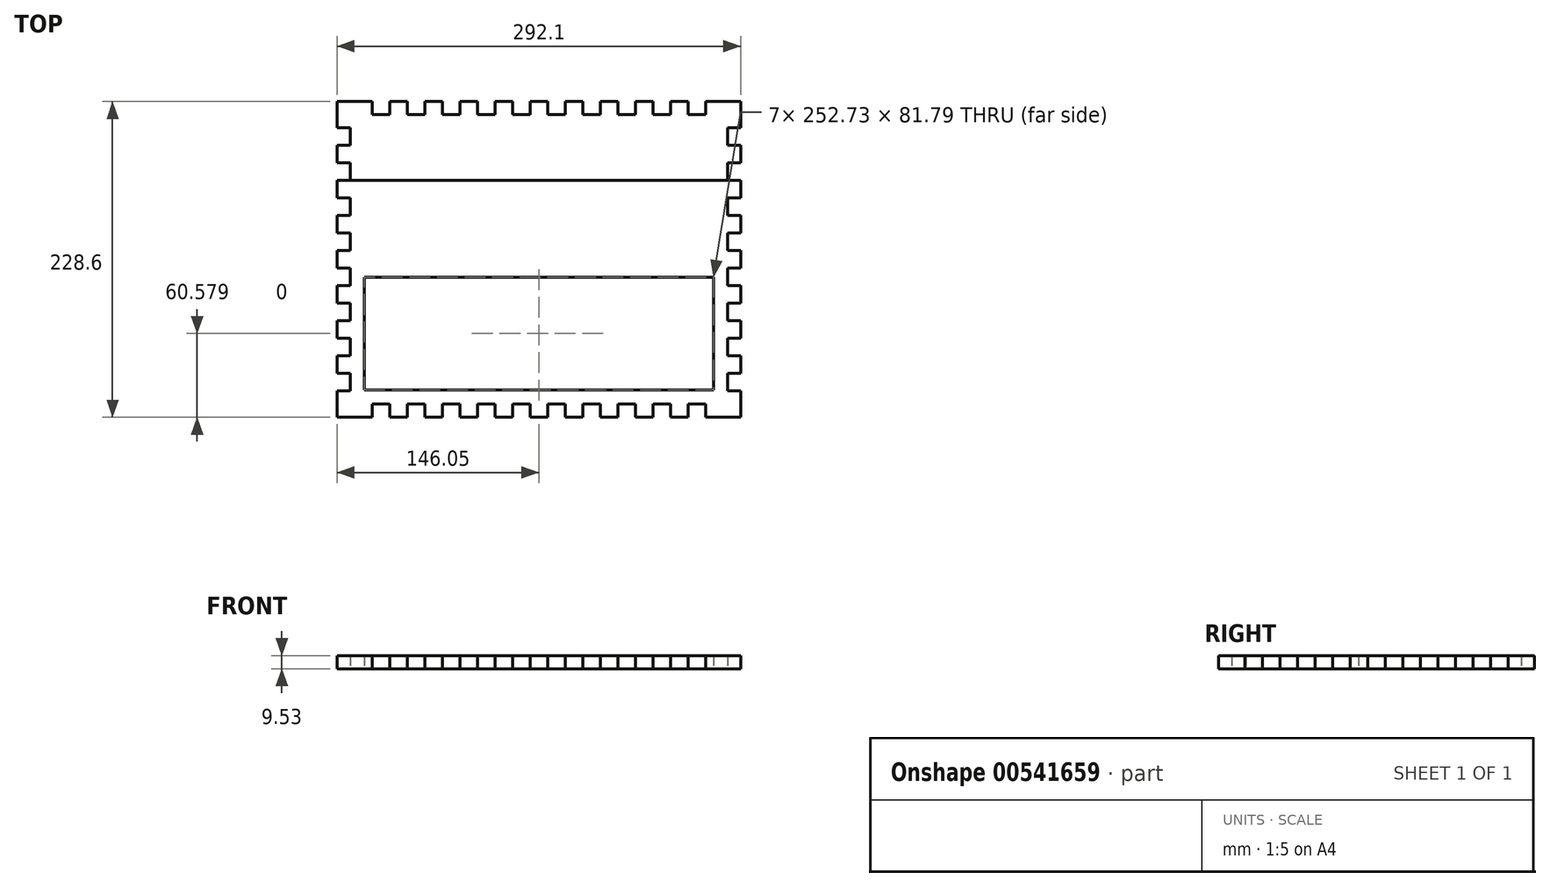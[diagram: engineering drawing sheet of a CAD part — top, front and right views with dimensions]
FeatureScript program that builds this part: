
annotation { "Feature Type Name" : "Feature", "Feature Type Description" : "" }
export const myFeature = defineFeature(function(context is Context, id is Id, definition is map)
    precondition{}
    {
        {
            var Q0;
            Q0=qCreatedBy(makeId("Top.planeOp"),FACE);
            var sketch = newSketch(context, id + "F0", { "sketchPlane" : qUnion([Q0])});
            skLineSegment(sketch, "E0.bottom", {"start": v(0, 0) * mm, "end": v(25.4, 0) * mm});
            skLineSegment(sketch, "E0.left", {"start": v(0, 0) * mm, "end": v(0, -19.05) * mm});
            skLineSegment(sketch, "E1", {"start": v(25.4, 0) * mm, "end": v(25.4, -9.53) * mm});
            skLineSegment(sketch, "E2", {"start": v(25.4, -9.53) * mm, "end": v(38.1, -9.53) * mm});
            skLineSegment(sketch, "E3", {"start": v(38.1, -9.53) * mm, "end": v(38.1, 0) * mm});
            skLineSegment(sketch, "E4", {"start": v(38.1, 0) * mm, "end": v(50.8, 0) * mm});
            skLineSegment(sketch, "E5", {"start": v(50.8, 0) * mm, "end": v(50.8, -9.53) * mm});
            skLineSegment(sketch, "E6", {"start": v(50.8, -9.53) * mm, "end": v(63.5, -9.53) * mm});
            skLineSegment(sketch, "E7", {"start": v(63.5, -9.53) * mm, "end": v(63.5, 0) * mm});
            skLineSegment(sketch, "E8", {"start": v(63.5, 0) * mm, "end": v(76.2, 0) * mm});
            skLineSegment(sketch, "E9", {"start": v(76.2, 0) * mm, "end": v(76.2, -9.52) * mm});
            skLineSegment(sketch, "E10", {"start": v(76.2, -9.52) * mm, "end": v(88.9, -9.52) * mm});
            skLineSegment(sketch, "E11", {"start": v(88.9, -9.52) * mm, "end": v(88.9, 0) * mm});
            skLineSegment(sketch, "E12", {"start": v(88.9, 0) * mm, "end": v(101.6, 0) * mm});
            skLineSegment(sketch, "E13", {"start": v(101.6, 0) * mm, "end": v(101.6, -9.52) * mm});
            skLineSegment(sketch, "E14", {"start": v(101.6, -9.52) * mm, "end": v(114.3, -9.52) * mm});
            skLineSegment(sketch, "E15", {"start": v(114.3, -9.52) * mm, "end": v(114.3, 0) * mm});
            skLineSegment(sketch, "E16.trimOffspring", {"start": v(114.3, 0) * mm, "end": v(127, 0) * mm});
            skLineSegment(sketch, "E17", {"start": v(127, 0) * mm, "end": v(127, -9.53) * mm});
            skLineSegment(sketch, "E18", {"start": v(127, -9.53) * mm, "end": v(139.7, -9.53) * mm});
            skLineSegment(sketch, "E19", {"start": v(139.7, -9.53) * mm, "end": v(139.7, 0) * mm});
            skLineSegment(sketch, "E20", {"start": v(139.7, 0) * mm, "end": v(152.4, 0) * mm});
            skLineSegment(sketch, "E21", {"start": v(152.4, 0) * mm, "end": v(152.4, -9.53) * mm});
            skLineSegment(sketch, "E22", {"start": v(152.4, -9.53) * mm, "end": v(165.1, -9.53) * mm});
            skLineSegment(sketch, "E23", {"start": v(165.1, -9.53) * mm, "end": v(165.1, 0) * mm});
            skLineSegment(sketch, "E24", {"start": v(165.1, 0) * mm, "end": v(177.8, 0) * mm});
            skLineSegment(sketch, "E25", {"start": v(177.8, 0) * mm, "end": v(177.8, -9.53) * mm});
            skLineSegment(sketch, "E26", {"start": v(177.8, -9.53) * mm, "end": v(190.5, -9.53) * mm});
            skLineSegment(sketch, "E27", {"start": v(190.5, -9.53) * mm, "end": v(190.5, 0) * mm});
            skLineSegment(sketch, "E28.trimOffspring", {"start": v(190.5, 0) * mm, "end": v(203.2, 0) * mm});
            skLineSegment(sketch, "E29", {"start": v(203.2, 0) * mm, "end": v(203.2, -9.53) * mm});
            skLineSegment(sketch, "E30", {"start": v(203.2, -9.53) * mm, "end": v(215.9, -9.53) * mm});
            skLineSegment(sketch, "E31", {"start": v(215.9, -9.53) * mm, "end": v(215.9, 0) * mm});
            skLineSegment(sketch, "E32", {"start": v(215.9, 0) * mm, "end": v(228.6, 0) * mm});
            skLineSegment(sketch, "E33", {"start": v(228.6, 0) * mm, "end": v(228.6, -9.53) * mm});
            skLineSegment(sketch, "E34", {"start": v(228.6, -9.53) * mm, "end": v(241.3, -9.53) * mm});
            skLineSegment(sketch, "E35", {"start": v(241.3, -9.53) * mm, "end": v(241.3, 0) * mm});
            skLineSegment(sketch, "E36", {"start": v(241.3, 0) * mm, "end": v(254, 0) * mm});
            skLineSegment(sketch, "E37", {"start": v(254, 0) * mm, "end": v(254, -9.53) * mm});
            skLineSegment(sketch, "E38", {"start": v(254, -9.53) * mm, "end": v(266.7, -9.53) * mm});
            skLineSegment(sketch, "E39", {"start": v(266.7, -9.53) * mm, "end": v(266.7, 0) * mm});
            skLineSegment(sketch, "E40.trimOffspring", {"start": v(266.7, 0) * mm, "end": v(292.1, 0) * mm});
            skLineSegment(sketch, "E41", {"start": v(0, -19.05) * mm, "end": v(9.52, -19.05) * mm});
            skLineSegment(sketch, "E42", {"start": v(9.52, -19.05) * mm, "end": v(9.52, -31.75) * mm});
            skLineSegment(sketch, "E43", {"start": v(9.52, -31.75) * mm, "end": v(0, -31.75) * mm});
            skLineSegment(sketch, "E44", {"start": v(0, -31.75) * mm, "end": v(0, -44.45) * mm});
            skLineSegment(sketch, "E45", {"start": v(0, -44.45) * mm, "end": v(9.53, -44.45) * mm});
            skLineSegment(sketch, "E46", {"start": v(9.53, -44.45) * mm, "end": v(9.53, -57.15) * mm});
            skLineSegment(sketch, "E47", {"start": v(9.53, -57.15) * mm, "end": v(0, -57.15) * mm});
            skLineSegment(sketch, "E48", {"start": v(0, -57.15) * mm, "end": v(0, -69.85) * mm});
            skLineSegment(sketch, "E49", {"start": v(0, -69.85) * mm, "end": v(9.53, -69.85) * mm});
            skLineSegment(sketch, "E50", {"start": v(9.53, -69.85) * mm, "end": v(9.53, -82.55) * mm});
            skLineSegment(sketch, "E51", {"start": v(9.53, -82.55) * mm, "end": v(0, -82.55) * mm});
            skLineSegment(sketch, "E52", {"start": v(0, -82.55) * mm, "end": v(0, -95.25) * mm});
            skLineSegment(sketch, "E53", {"start": v(0, -95.25) * mm, "end": v(9.53, -95.25) * mm});
            skLineSegment(sketch, "E54", {"start": v(9.53, -95.25) * mm, "end": v(9.53, -107.95) * mm});
            skLineSegment(sketch, "E55", {"start": v(9.53, -107.95) * mm, "end": v(0, -107.95) * mm});
            skLineSegment(sketch, "E56.trimOffspring", {"start": v(0, -107.95) * mm, "end": v(0, -120.65) * mm});
            skLineSegment(sketch, "E57", {"start": v(0, -120.65) * mm, "end": v(9.53, -120.65) * mm});
            skLineSegment(sketch, "E58", {"start": v(9.53, -120.65) * mm, "end": v(9.53, -133.35) * mm});
            skLineSegment(sketch, "E59", {"start": v(9.53, -133.35) * mm, "end": v(0, -133.35) * mm});
            skLineSegment(sketch, "E60", {"start": v(0, -133.35) * mm, "end": v(0, -146.05) * mm});
            skLineSegment(sketch, "E61", {"start": v(0, -146.05) * mm, "end": v(9.53, -146.05) * mm});
            skLineSegment(sketch, "E62", {"start": v(9.53, -146.05) * mm, "end": v(9.53, -158.75) * mm});
            skLineSegment(sketch, "E63", {"start": v(9.53, -158.75) * mm, "end": v(0, -158.75) * mm});
            skLineSegment(sketch, "E64", {"start": v(0, -158.75) * mm, "end": v(0, -171.45) * mm});
            skLineSegment(sketch, "E65", {"start": v(0, -171.45) * mm, "end": v(9.53, -171.45) * mm});
            skLineSegment(sketch, "E66", {"start": v(9.53, -171.45) * mm, "end": v(9.53, -184.15) * mm});
            skLineSegment(sketch, "E67", {"start": v(9.53, -184.15) * mm, "end": v(0, -184.15) * mm});
            skLineSegment(sketch, "E68.trimOffspring", {"start": v(0, -184.15) * mm, "end": v(0, -196.85) * mm});
            skLineSegment(sketch, "E69", {"start": v(0, -196.85) * mm, "end": v(9.53, -196.85) * mm});
            skLineSegment(sketch, "E70", {"start": v(9.53, -196.85) * mm, "end": v(9.53, -209.55) * mm});
            skLineSegment(sketch, "E71", {"start": v(9.53, -209.55) * mm, "end": v(0, -209.55) * mm});
            skLineSegment(sketch, "E72.trimOffspring", {"start": v(0, -209.55) * mm, "end": v(0, -228.6) * mm});
            skLineSegment(sketch, "E73", {"start": v(146.05, 0) * mm, "end": v(146.05, -86.34) * mm, "construction": true});
            skLineSegment(sketch, "E74", {"start": v(0, -114.3) * mm, "end": v(52.01, -114.3) * mm, "construction": true});
            skLineSegment(sketch, "E75.MirrorCS", {"start": v(292.1, 0) * mm, "end": v(292.1, -19.05) * mm});
            skLineSegment(sketch, "E76.MirrorCS", {"start": v(292.1, -19.05) * mm, "end": v(282.57, -19.05) * mm});
            skLineSegment(sketch, "E77.MirrorCS", {"start": v(282.57, -19.05) * mm, "end": v(282.57, -31.75) * mm});
            skLineSegment(sketch, "E78.MirrorCS", {"start": v(282.57, -31.75) * mm, "end": v(292.1, -31.75) * mm});
            skLineSegment(sketch, "E79.MirrorCS", {"start": v(292.1, -31.75) * mm, "end": v(292.1, -44.45) * mm});
            skLineSegment(sketch, "E80.MirrorCS", {"start": v(292.1, -44.45) * mm, "end": v(282.57, -44.45) * mm});
            skLineSegment(sketch, "E81.MirrorCS", {"start": v(282.57, -44.45) * mm, "end": v(282.57, -57.15) * mm});
            skLineSegment(sketch, "E82.MirrorCS", {"start": v(282.57, -57.15) * mm, "end": v(292.1, -57.15) * mm});
            skLineSegment(sketch, "E83.MirrorCS", {"start": v(292.1, -57.15) * mm, "end": v(292.1, -69.85) * mm});
            skLineSegment(sketch, "E84.MirrorCS", {"start": v(292.1, -69.85) * mm, "end": v(282.57, -69.85) * mm});
            skLineSegment(sketch, "E85.MirrorCS", {"start": v(282.57, -69.85) * mm, "end": v(282.57, -82.55) * mm});
            skLineSegment(sketch, "E86.MirrorCS", {"start": v(282.57, -107.95) * mm, "end": v(292.1, -107.95) * mm});
            skLineSegment(sketch, "E87.MirrorCS", {"start": v(292.1, -107.95) * mm, "end": v(292.1, -120.65) * mm});
            skLineSegment(sketch, "E88.MirrorCS", {"start": v(292.1, -120.65) * mm, "end": v(282.57, -120.65) * mm});
            skLineSegment(sketch, "E89.MirrorCS", {"start": v(282.57, -120.65) * mm, "end": v(282.57, -133.35) * mm});
            skLineSegment(sketch, "E90.MirrorCS", {"start": v(282.57, -133.35) * mm, "end": v(292.1, -133.35) * mm});
            skLineSegment(sketch, "E91.MirrorCS", {"start": v(292.1, -133.35) * mm, "end": v(292.1, -146.05) * mm});
            skLineSegment(sketch, "E92.MirrorCS", {"start": v(292.1, -146.05) * mm, "end": v(282.57, -146.05) * mm});
            skLineSegment(sketch, "E93.MirrorCS", {"start": v(282.57, -146.05) * mm, "end": v(282.57, -158.75) * mm});
            skLineSegment(sketch, "E94.MirrorCS", {"start": v(282.57, -158.75) * mm, "end": v(292.1, -158.75) * mm});
            skLineSegment(sketch, "E95.MirrorCS", {"start": v(292.1, -158.75) * mm, "end": v(292.1, -171.45) * mm});
            skLineSegment(sketch, "E96.MirrorCS", {"start": v(292.1, -171.45) * mm, "end": v(282.57, -171.45) * mm});
            skLineSegment(sketch, "E97.MirrorCS", {"start": v(282.57, -171.45) * mm, "end": v(282.57, -184.15) * mm});
            skLineSegment(sketch, "E98.MirrorCS", {"start": v(282.57, -184.15) * mm, "end": v(292.1, -184.15) * mm});
            skLineSegment(sketch, "E99.MirrorCS", {"start": v(292.1, -184.15) * mm, "end": v(292.1, -196.85) * mm});
            skLineSegment(sketch, "E100.MirrorCS", {"start": v(292.1, -196.85) * mm, "end": v(282.57, -196.85) * mm});
            skLineSegment(sketch, "E101.MirrorCS", {"start": v(282.57, -196.85) * mm, "end": v(282.57, -209.55) * mm});
            skLineSegment(sketch, "E102.MirrorCS", {"start": v(282.57, -209.55) * mm, "end": v(292.1, -209.55) * mm});
            skLineSegment(sketch, "E103.MirrorCS", {"start": v(292.1, -209.55) * mm, "end": v(292.1, -228.6) * mm});
            skLineSegment(sketch, "E104.MirrorCS", {"start": v(282.57, -82.55) * mm, "end": v(292.1, -82.55) * mm});
            skLineSegment(sketch, "E105.MirrorCS", {"start": v(292.1, -82.55) * mm, "end": v(292.1, -95.25) * mm});
            skLineSegment(sketch, "E106.MirrorCS", {"start": v(282.57, -95.25) * mm, "end": v(282.57, -107.95) * mm});
            skLineSegment(sketch, "E107.MirrorCS", {"start": v(292.1, -95.25) * mm, "end": v(282.57, -95.25) * mm});
            skLineSegment(sketch, "E108.MirrorCS", {"start": v(0, -228.6) * mm, "end": v(25.4, -228.6) * mm});
            skLineSegment(sketch, "E109.MirrorCS", {"start": v(25.4, -228.6) * mm, "end": v(25.4, -219.08) * mm});
            skLineSegment(sketch, "E110.MirrorCS", {"start": v(25.4, -219.08) * mm, "end": v(38.1, -219.08) * mm});
            skLineSegment(sketch, "E111.MirrorCS", {"start": v(38.1, -219.08) * mm, "end": v(38.1, -228.6) * mm});
            skLineSegment(sketch, "E112.MirrorCS", {"start": v(38.1, -228.6) * mm, "end": v(50.8, -228.6) * mm});
            skLineSegment(sketch, "E113.MirrorCS", {"start": v(50.8, -228.6) * mm, "end": v(50.8, -219.08) * mm});
            skLineSegment(sketch, "E114.MirrorCS", {"start": v(50.8, -219.08) * mm, "end": v(63.5, -219.08) * mm});
            skLineSegment(sketch, "E115.MirrorCS", {"start": v(63.5, -219.08) * mm, "end": v(63.5, -228.6) * mm});
            skLineSegment(sketch, "E116.MirrorCS", {"start": v(63.5, -228.6) * mm, "end": v(76.2, -228.6) * mm});
            skLineSegment(sketch, "E117.MirrorCS", {"start": v(76.2, -228.6) * mm, "end": v(76.2, -219.08) * mm});
            skLineSegment(sketch, "E118.MirrorCS", {"start": v(76.2, -219.08) * mm, "end": v(88.9, -219.08) * mm});
            skLineSegment(sketch, "E119.MirrorCS", {"start": v(88.9, -219.08) * mm, "end": v(88.9, -228.6) * mm});
            skLineSegment(sketch, "E120.MirrorCS", {"start": v(88.9, -228.6) * mm, "end": v(101.6, -228.6) * mm});
            skLineSegment(sketch, "E121.MirrorCS", {"start": v(101.6, -228.6) * mm, "end": v(101.6, -219.08) * mm});
            skLineSegment(sketch, "E122.MirrorCS", {"start": v(101.6, -219.08) * mm, "end": v(114.3, -219.08) * mm});
            skLineSegment(sketch, "E123.MirrorCS", {"start": v(114.3, -219.08) * mm, "end": v(114.3, -228.6) * mm});
            skLineSegment(sketch, "E124.MirrorCS", {"start": v(114.3, -228.6) * mm, "end": v(127, -228.6) * mm});
            skLineSegment(sketch, "E125.MirrorCS", {"start": v(127, -228.6) * mm, "end": v(127, -219.08) * mm});
            skLineSegment(sketch, "E126.MirrorCS", {"start": v(127, -219.08) * mm, "end": v(139.7, -219.08) * mm});
            skLineSegment(sketch, "E127.MirrorCS", {"start": v(139.7, -219.08) * mm, "end": v(139.7, -228.6) * mm});
            skLineSegment(sketch, "E128.MirrorCS", {"start": v(139.7, -228.6) * mm, "end": v(152.4, -228.6) * mm});
            skLineSegment(sketch, "E129.MirrorCS", {"start": v(152.4, -228.6) * mm, "end": v(152.4, -219.08) * mm});
            skLineSegment(sketch, "E130.MirrorCS", {"start": v(152.4, -219.08) * mm, "end": v(165.1, -219.08) * mm});
            skLineSegment(sketch, "E131.MirrorCS", {"start": v(165.1, -219.08) * mm, "end": v(165.1, -228.6) * mm});
            skLineSegment(sketch, "E132.MirrorCS", {"start": v(165.1, -228.6) * mm, "end": v(177.8, -228.6) * mm});
            skLineSegment(sketch, "E133.MirrorCS", {"start": v(177.8, -228.6) * mm, "end": v(177.8, -219.08) * mm});
            skLineSegment(sketch, "E134.MirrorCS", {"start": v(177.8, -219.08) * mm, "end": v(190.5, -219.08) * mm});
            skLineSegment(sketch, "E135.MirrorCS", {"start": v(190.5, -219.08) * mm, "end": v(190.5, -228.6) * mm});
            skLineSegment(sketch, "E136.MirrorCS", {"start": v(190.5, -228.6) * mm, "end": v(203.2, -228.6) * mm});
            skLineSegment(sketch, "E137.MirrorCS", {"start": v(203.2, -228.6) * mm, "end": v(203.2, -219.08) * mm});
            skLineSegment(sketch, "E138.MirrorCS", {"start": v(203.2, -219.08) * mm, "end": v(215.9, -219.08) * mm});
            skLineSegment(sketch, "E139.MirrorCS", {"start": v(215.9, -219.08) * mm, "end": v(215.9, -228.6) * mm});
            skLineSegment(sketch, "E140.MirrorCS", {"start": v(215.9, -228.6) * mm, "end": v(228.6, -228.6) * mm});
            skLineSegment(sketch, "E141.MirrorCS", {"start": v(228.6, -228.6) * mm, "end": v(228.6, -219.08) * mm});
            skLineSegment(sketch, "E142.MirrorCS", {"start": v(228.6, -219.08) * mm, "end": v(241.3, -219.08) * mm});
            skLineSegment(sketch, "E143.MirrorCS", {"start": v(241.3, -219.08) * mm, "end": v(241.3, -228.6) * mm});
            skLineSegment(sketch, "E144.MirrorCS", {"start": v(241.3, -228.6) * mm, "end": v(254, -228.6) * mm});
            skLineSegment(sketch, "E145.MirrorCS", {"start": v(254, -228.6) * mm, "end": v(254, -219.08) * mm});
            skLineSegment(sketch, "E146.MirrorCS", {"start": v(254, -219.08) * mm, "end": v(266.7, -219.08) * mm});
            skLineSegment(sketch, "E147.MirrorCS", {"start": v(266.7, -219.08) * mm, "end": v(266.7, -228.6) * mm});
            skLineSegment(sketch, "E148.MirrorCS", {"start": v(266.7, -228.6) * mm, "end": v(292.1, -228.6) * mm});
            skLineSegment(sketch, "E149", {"start": v(9.53, -57.15) * mm, "end": v(282.57, -57.15) * mm});
            skLineSegment(sketch, "E150.bottom", {"start": v(19.69, -127.13) * mm, "end": v(272.41, -127.13) * mm});
            skLineSegment(sketch, "E150.top", {"start": v(19.69, -208.92) * mm, "end": v(272.41, -208.92) * mm});
            skLineSegment(sketch, "E150.left", {"start": v(19.69, -127.13) * mm, "end": v(19.69, -208.92) * mm});
            skLineSegment(sketch, "E150.right", {"start": v(272.41, -127.13) * mm, "end": v(272.41, -208.92) * mm});
            skSolve(sketch);
        }
        {
            var Q0;
            Q0=makeQuery(id+"F0.imprint","IMPRINT",FACE,{"disambiguationData":[TD([[makeQuery(id+"F0.imprint","IMPRINT",EDGE,{"derivedFrom":sQuery(id+"F0.wireOp",EDGE,"E0.bottom")}),-1.0]])]});
            extrude(context, id + "F1", {"entities" : qUnion([Q0]), "depth" : 9.52 * mm, "offsetDistance" : 25.4 * mm});
        }
        {
            var Q0;
            Q0=makeQuery(id+"F0.imprint","IMPRINT",FACE,{"disambiguationData":[TD([[makeQuery(id+"F0.imprint","IMPRINT",EDGE,{"derivedFrom":sQuery(id+"F0.wireOp",EDGE,"E47")}),1.0]])]});
            extrude(context, id + "F2", {"entities" : qUnion([Q0]), "depth" : 9.52 * mm, "offsetDistance" : 25.4 * mm});
        }
    });
